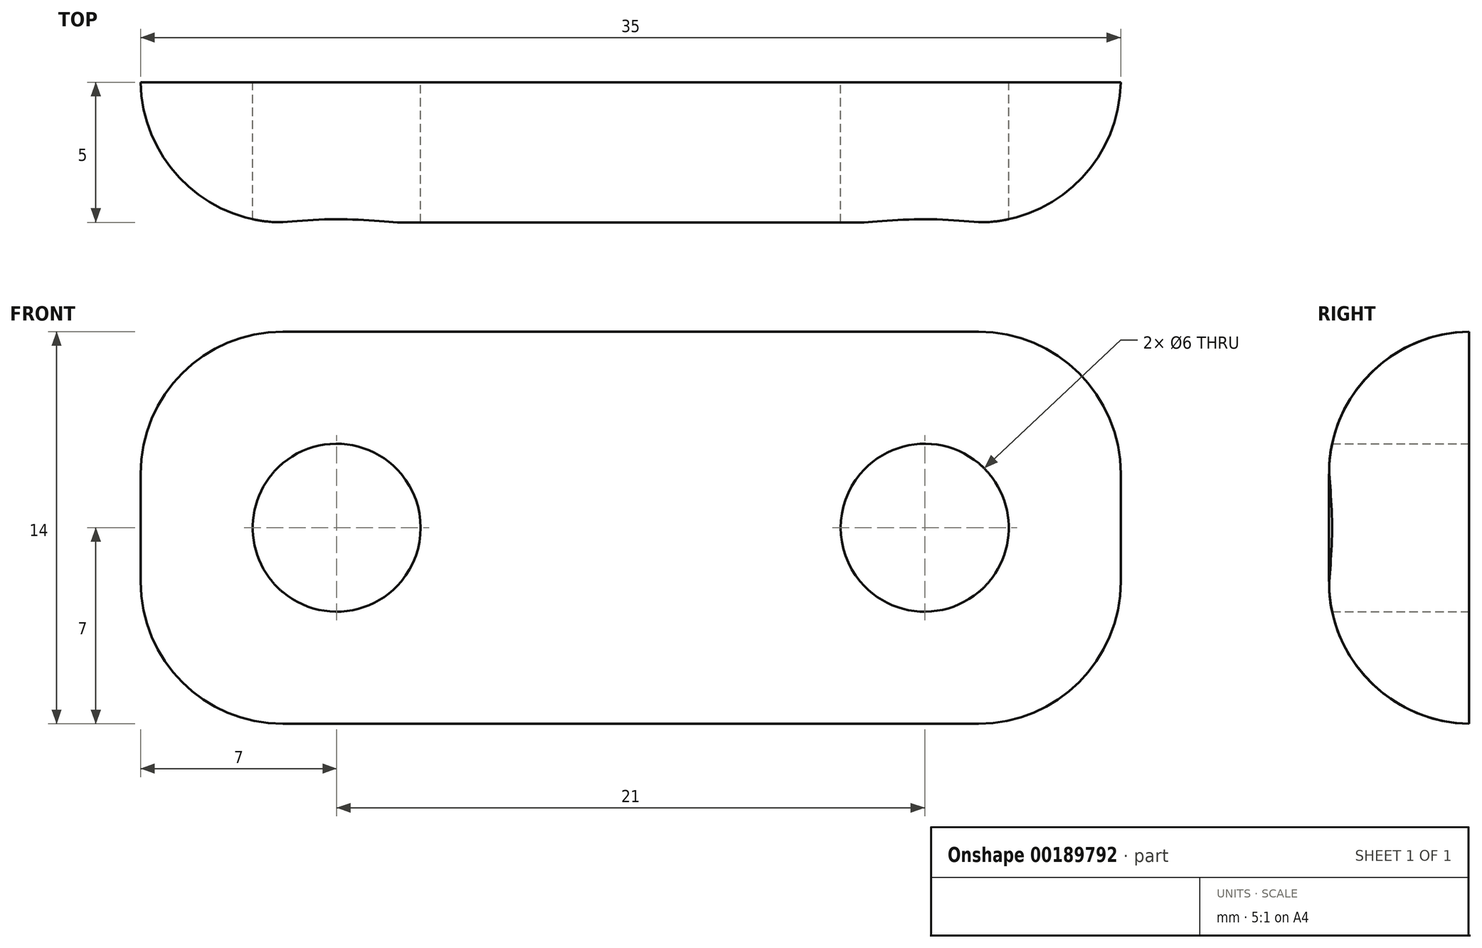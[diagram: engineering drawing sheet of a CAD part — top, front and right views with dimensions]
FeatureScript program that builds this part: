
annotation { "Feature Type Name" : "Feature", "Feature Type Description" : "" }
export const myFeature = defineFeature(function(context is Context, id is Id, definition is map)
    precondition{}
    {
        {
            var Q0;
            Q0=qCreatedBy(makeId("Front.planeOp"),FACE);
            var sketch = newSketch(context, id + "F0", { "sketchPlane" : qUnion([Q0])});
            skLineSegment(sketch, "E0.bottom", {"start": v(0, 0) * mm, "end": v(35, 0) * mm});
            skLineSegment(sketch, "E0.top", {"start": v(0, 14) * mm, "end": v(35, 14) * mm});
            skLineSegment(sketch, "E0.left", {"start": v(0, 0) * mm, "end": v(0, 14) * mm});
            skLineSegment(sketch, "E0.right", {"start": v(35, 0) * mm, "end": v(35, 14) * mm});
            skLineSegment(sketch, "E1", {"start": v(35, 7) * mm, "end": v(0, 7) * mm, "construction": true});
            skLineSegment(sketch, "E2", {"start": v(0, 7) * mm, "end": v(7, 7) * mm, "construction": true});
            skCircle(sketch, "E3", {"center": v(7, 7) * mm, "radius": 3 * mm});
            skLineSegment(sketch, "E4", {"start": v(35, 7) * mm, "end": v(28, 7) * mm, "construction": true});
            skCircle(sketch, "E5", {"center": v(28, 7) * mm, "radius": 3 * mm});
            skSolve(sketch);
        }
        {
            var Q0;
            Q0=makeQuery(id+"F0.imprint","IMPRINT",FACE,{"disambiguationData":[TD([[makeQuery(id+"F0.imprint","IMPRINT",EDGE,{"derivedFrom":sQuery(id+"F0.wireOp",EDGE,"E0.bottom")}),1.0]])]});
            extrude(context, id + "F1", {"entities" : qUnion([Q0]), "depth" : 5 * mm});
        }
        {
            var Q0;
            Q0=makeQuery(id+"F1.opExtrude","SWEPT_EDGE",EDGE,{"disambiguationData":[OSD([sQuery(id+"F0.wireOp",EDGE,"E0.top"),sQuery(id+"F0.wireOp",EDGE,"E0.right")])]});
            var Q1;
            Q1=makeQuery(id+"F1.opExtrude","SWEPT_EDGE",EDGE,{"disambiguationData":[OSD([sQuery(id+"F0.wireOp",EDGE,"E0.bottom"),sQuery(id+"F0.wireOp",EDGE,"E0.right")])]});
            var Q2;
            Q2=makeQuery(id+"F1.opExtrude","SWEPT_EDGE",EDGE,{"disambiguationData":[OSD([sQuery(id+"F0.wireOp",EDGE,"E0.bottom"),sQuery(id+"F0.wireOp",EDGE,"E0.left")])]});
            var Q3;
            Q3=makeQuery(id+"F1.opExtrude","SWEPT_EDGE",EDGE,{"disambiguationData":[OSD([sQuery(id+"F0.wireOp",EDGE,"E0.top"),sQuery(id+"F0.wireOp",EDGE,"E0.left")])]});
            fillet(context, id + "F2", {"entities" : qUnion([Q0, Q1, Q2, Q3]), "radius" : 5.08 * mm, "tangentPropagation" : true, "allowEdgeOverflow" : false});
        }
        {
            var Q0;
            Q0=makeQuery(id+"F1.opExtrude","CAP_EDGE",EDGE,{"disambiguationData":[OSD([sQuery(id+"F0.wireOp",EDGE,"E0.top")])],"isStart":false});
            fillet(context, id + "F3", {"entities" : qUnion([Q0]), "radius" : 5.08 * mm, "tangentPropagation" : true, "allowEdgeOverflow" : false});
        }
    });
